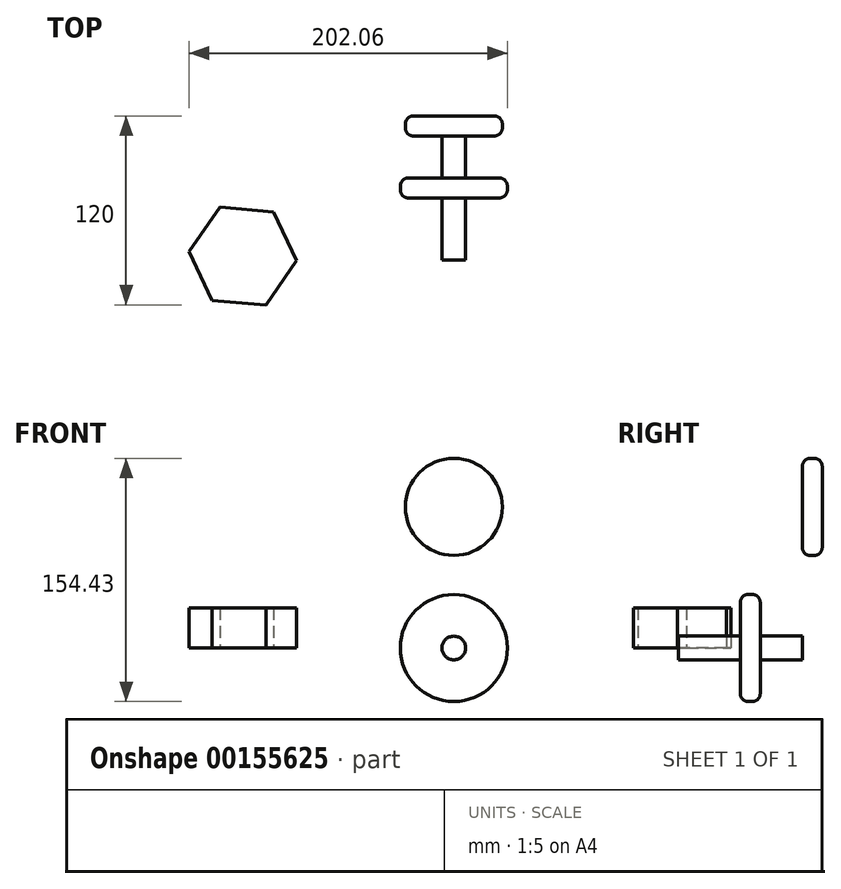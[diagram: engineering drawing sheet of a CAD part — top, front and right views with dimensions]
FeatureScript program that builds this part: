
annotation { "Feature Type Name" : "Feature", "Feature Type Description" : "" }
export const myFeature = defineFeature(function(context is Context, id is Id, definition is map)
    precondition{}
    {
        {
            var Q0;
            Q0=qCreatedBy(makeId("Front.planeOp"),FACE);
            var sketch = newSketch(context, id + "F0", { "sketchPlane" : qUnion([Q0])});
            skCircle(sketch, "E0", {"center": v(0, 0) * mm, "radius": 34 * mm});
            skSolve(sketch);
        }
        {
            var Q0;
            Q0=makeQuery(id+"F0.imprint","IMPRINT",FACE,{"disambiguationData":[TD([[makeQuery(id+"F0.imprint","IMPRINT",EDGE,{"derivedFrom":sQuery(id+"F0.wireOp",EDGE,"E0")}),1.0]])]});
            extrude(context, id + "F1", {"entities" : qUnion([Q0]), "depth" : 12.7 * mm});
        }
        {
            var Q0;
            Q0=makeQuery(id+"F1.opExtrude","CAP_EDGE",EDGE,{"disambiguationData":[OSD([sQuery(id+"F0.wireOp",EDGE,"E0")])],"isStart":false});
            var Q1;
            Q1=makeQuery(id+"F1.opExtrude","CAP_EDGE",EDGE,{"disambiguationData":[OSD([sQuery(id+"F0.wireOp",EDGE,"E0")])],"isStart":true});
            var Q2;
            Q2=makeQuery(id+"F1.opExtrude","CAP_FACE",FACE,{"disambiguationData":[OSD([sQuery(id+"F0.wireOp",EDGE,"E0")])],"isStart":false});
            fillet(context, id + "F2", {"entities" : qUnion([Q0, Q1, Q2]), "radius" : 5.08 * mm, "tangentPropagation" : true, "allowEdgeOverflow" : false});
        }
        {
            var Q0;
            Q0=makeQuery(id+"F1.opExtrude","CAP_FACE",FACE,{"disambiguationData":[OSD([sQuery(id+"F0.wireOp",EDGE,"E0")])],"isStart":false});
            var sketch = newSketch(context, id + "F3", { "sketchPlane" : qUnion([Q0])});
            skCircle(sketch, "E1", {"center": v(0, 0) * mm, "radius": 7.54 * mm});
            skSolve(sketch);
        }
        {
            var Q0;
            Q0=makeQuery(id+"F3.imprint","IMPRINT",FACE,{"disambiguationData":[TD([[makeQuery(id+"F3.imprint","IMPRINT",EDGE,{"derivedFrom":sQuery(id+"F3.wireOp",EDGE,"E1")}),1.0]])]});
            extrude(context, id + "F4", {"entities" : qUnion([Q0]), "operationType" : NewBodyOperationType.ADD, "endBound" : BoundingType.SYMMETRIC, "oppositeDirection" : true, "depth" : 78.74 * mm});
        }
        {
            var Q0;
            Q0=qCreatedBy(makeId("Top.planeOp"),FACE);
            var sketch = newSketch(context, id + "F5", { "sketchPlane" : qUnion([Q0])});
            skCircle(sketch, "E2.cCircle", {"center": v(-133.94, -49.62) * mm, "radius": 29.67 * mm, "construction": true});
            skLineSegment(sketch, "E2.0", {"start": v(-114.37, -21.5) * mm, "end": v(-99.8, -52.52) * mm});
            skLineSegment(sketch, "E2.1", {"start": v(-99.8, -52.52) * mm, "end": v(-119.37, -80.63) * mm});
            skLineSegment(sketch, "E2.2", {"start": v(-119.37, -80.63) * mm, "end": v(-153.5, -77.74) * mm});
            skLineSegment(sketch, "E2.3", {"start": v(-153.5, -77.74) * mm, "end": v(-168.07, -46.73) * mm});
            skLineSegment(sketch, "E2.4", {"start": v(-168.07, -46.73) * mm, "end": v(-148.5, -18.62) * mm});
            skLineSegment(sketch, "E2.5", {"start": v(-148.5, -18.62) * mm, "end": v(-114.37, -21.5) * mm});
            skPoint(sketch, "E2.0.midPoint", {"position": v(-107.08, -37.01) * mm});
            skSolve(sketch);
        }
        {
            var Q0;
            Q0 = qSketchRegion(id + "F5", true);
            extrude(context, id + "F6", {"entities" : qUnion([Q0]), "operationType" : NewBodyOperationType.ADD, "depth" : 25.4 * mm});
        }
        {
            var Q0;
            Q0=makeQuery(id+"F4.opExtrude","CAP_FACE",FACE,{"disambiguationData":[OSD([sQuery(id+"F3.wireOp",EDGE,"E1")])],"isStart":false});
            var sketch = newSketch(context, id + "F7", { "sketchPlane" : qUnion([Q0])});
            skCircle(sketch, "E3", {"center": v(0, 89.63) * mm, "radius": 30.8 * mm});
            skSolve(sketch);
        }
        {
            var Q0;
            Q0=makeQuery(id+"F7.imprint","IMPRINT",FACE,{"disambiguationData":[TD([[makeQuery(id+"F7.imprint","IMPRINT",EDGE,{"derivedFrom":sQuery(id+"F7.wireOp",EDGE,"E3")}),1.0]])]});
            extrude(context, id + "F8", {"entities" : qUnion([Q0]), "depth" : 12.7 * mm});
        }
        {
            var Q0;
            Q0=makeQuery(id+"F8.opExtrude","CAP_FACE",FACE,{"disambiguationData":[OSD([sQuery(id+"F7.wireOp",EDGE,"E3")])],"isStart":false});
            var Q1;
            Q1=makeQuery(id+"F8.opExtrude","CAP_EDGE",EDGE,{"disambiguationData":[OSD([sQuery(id+"F7.wireOp",EDGE,"E3")])],"isStart":true});
            fillet(context, id + "F9", {"entities" : qUnion([Q0, Q1]), "radius" : 5.08 * mm, "tangentPropagation" : true, "allowEdgeOverflow" : false});
        }
    });
